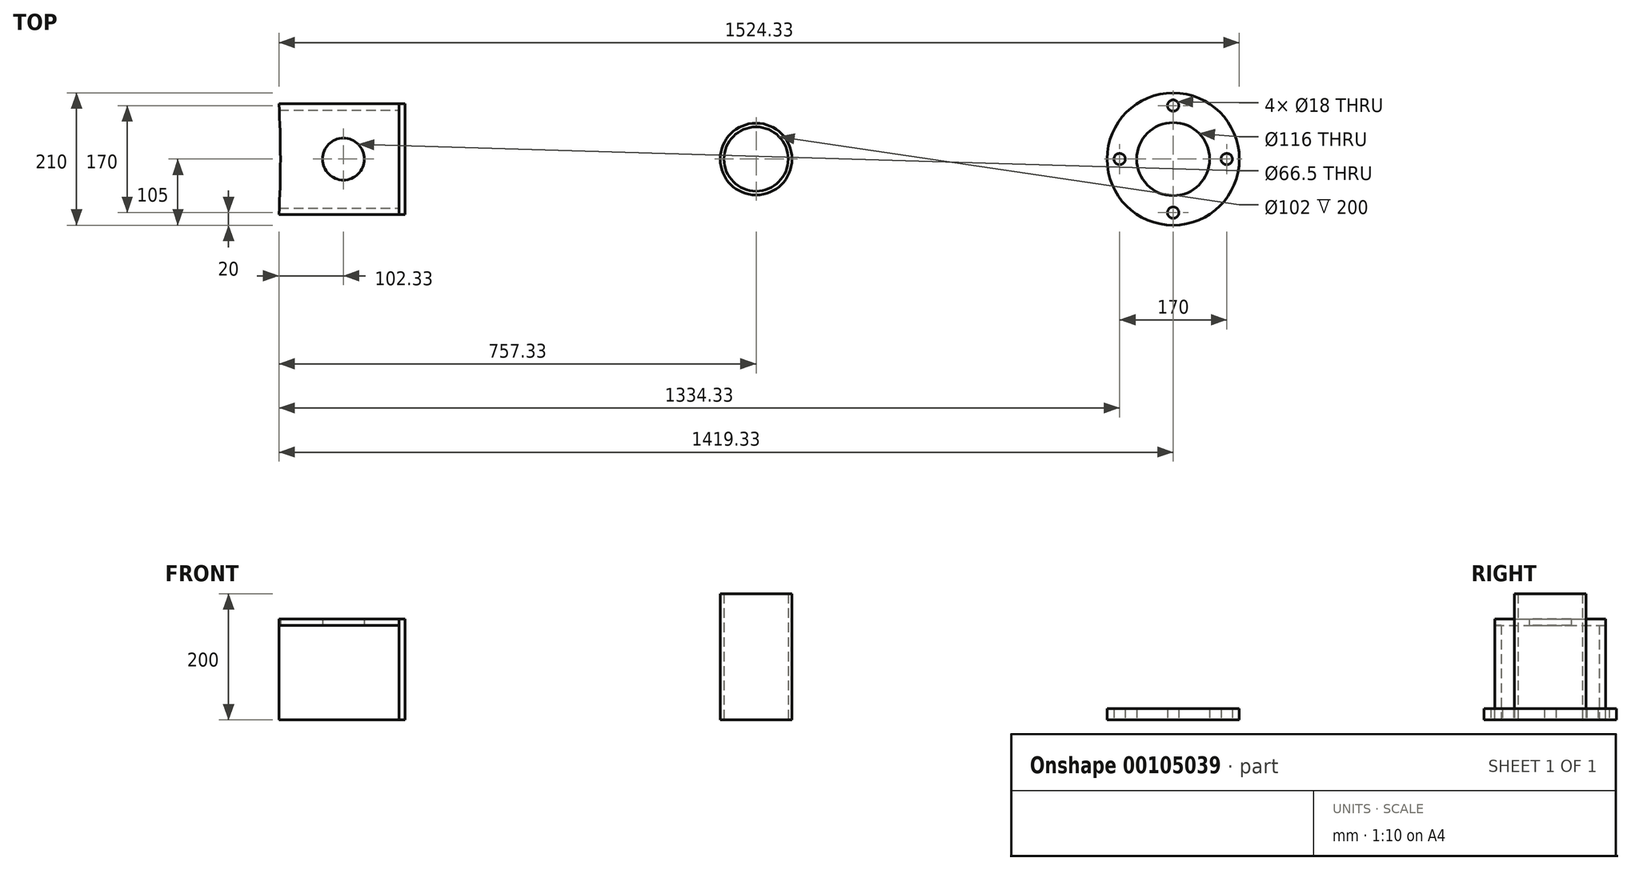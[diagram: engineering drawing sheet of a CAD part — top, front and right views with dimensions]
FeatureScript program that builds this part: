
annotation { "Feature Type Name" : "Feature", "Feature Type Description" : "" }
export const myFeature = defineFeature(function(context is Context, id is Id, definition is map)
    precondition{}
    {
        {
            var Q0;
            Q0=qCreatedBy(makeId("Top.planeOp"),FACE);
            var sketch = newSketch(context, id + "F0", { "sketchPlane" : qUnion([Q0])});
            skCircle(sketch, "E0", {"center": v(0, 0) * mm, "radius": 1665 * mm});
            skLineSegment(sketch, "E1", {"start": v(1663.17, 78) * mm, "end": v(1853, 78) * mm});
            skLineSegment(sketch, "E2", {"start": v(1853, 78) * mm, "end": v(1853, 88) * mm});
            skLineSegment(sketch, "E3", {"start": v(1853, 88) * mm, "end": v(1662.67, 88) * mm});
            skCircle(sketch, "E4", {"center": v(1765, 0) * mm, "radius": 58 * mm});
            skCircle(sketch, "E5", {"center": v(0, 0) * mm, "radius": 1677 * mm, "construction": true});
            skSolve(sketch);
        }
        {
            var Q0;
            {var subQ0=sQuery(id+"F0.wireOp",EDGE,"E1");Q0=makeQuery(id+"F0.imprint","IMPRINT",FACE,{"disambiguationData":[TD([[makeQuery(id+"F0.imprint","IMPRINT",EDGE,{"derivedFrom":subQ0}),1.0]])]});}
            extrude(context, id + "F1", {"entities" : qUnion([Q0]), "depth" : 150 * mm});
        }
        {
            var Q0;
            Q0=makeQuery(id+"F1.opExtrude","SWEPT_BODY",BODY,{"disambiguationData":[OSD([sQuery(id+"F0.wireOp",EDGE,"E0"),sQuery(id+"F0.wireOp",EDGE,"E1"),sQuery(id+"F0.wireOp",EDGE,"E2"),sQuery(id+"F0.wireOp",EDGE,"E3")])]});
            var Q1;
            Q1=qCreatedBy(makeId("Front.planeOp"),FACE);
            mirror(context, id + "F2", {"entities" : qUnion([Q0]), "mirrorPlane" : qUnion([Q1])});
        }
        {
            var Q0;
            Q0=makeQuery(id+"F1.opExtrude","CAP_FACE",FACE,{"disambiguationData":[OSD([sQuery(id+"F0.wireOp",EDGE,"E0"),sQuery(id+"F0.wireOp",EDGE,"E1"),sQuery(id+"F0.wireOp",EDGE,"E2"),sQuery(id+"F0.wireOp",EDGE,"E3")])],"isStart":false});
            var sketch = newSketch(context, id + "F3", { "sketchPlane" : qUnion([Q0])});
            skLineSegment(sketch, "E6", {"start": v(1662.67, 88) * mm, "end": v(1853, 88) * mm});
            skLineSegment(sketch, "E7", {"start": v(1853, 88) * mm, "end": v(1853, -88) * mm});
            skLineSegment(sketch, "E8", {"start": v(1853, -88) * mm, "end": v(1662.67, -88) * mm});
            skArc(sketch, "E9", {"start": v(1662.67, 88) * mm, "mid": v(1665, 0) * mm, "end": v(1662.67, -88) * mm});
            skCircle(sketch, "E10", {"center": v(1765, 0) * mm, "radius": 33.25 * mm});
            skSolve(sketch);
        }
        {
            var Q0;
            Q0=qSketchRegion(id+"F3",true);
            extrude(context, id + "F4", {"entities" : qUnion([Q0]), "depth" : 10 * mm});
        }
        {
            var Q0;
            Q0=makeQuery(id+"F2.opPattern","COPY",FACE,{"derivedFrom":makeQuery(id+"F1.opExtrude","SWEPT_FACE",FACE,{"disambiguationData":[OSD([sQuery(id+"F0.wireOp",EDGE,"E2")])]}),"instanceName":"1"});
            var sketch = newSketch(context, id + "F5", { "sketchPlane" : qUnion([Q0])});
            skLineSegment(sketch, "E11.bottom", {"start": v(-88, 0) * mm, "end": v(88, 0) * mm});
            skLineSegment(sketch, "E11.top", {"start": v(-88, 160) * mm, "end": v(88, 160) * mm});
            skLineSegment(sketch, "E11.left", {"start": v(-88, 0) * mm, "end": v(-88, 160) * mm});
            skLineSegment(sketch, "E11.right", {"start": v(88, 0) * mm, "end": v(88, 160) * mm});
            skSolve(sketch);
        }
        {
            var Q0;
            Q0=qSketchRegion(id+"F5",true);
            extrude(context, id + "F6", {"entities" : qUnion([Q0]), "depth" : 10 * mm});
        }
        {
            assignVariable(context, id + "F7", {"name" : "C6", "anyValue" : 18});
        }
        {
            assignVariable(context, id + "F8", {"name" : "C8", "anyValue" : 4});
        }
        {
            var Q0;
            Q0=qCreatedBy(makeId("Top.planeOp"),FACE);
            var sketch = newSketch(context, id + "F9", { "sketchPlane" : qUnion([Q0])});
            skCircle(sketch, "E12", {"center": v(2420, 0) * mm, "radius": 51 * mm});
            skCircle(sketch, "E13", {"center": v(2420, 0) * mm, "radius": 57 * mm});
            skCircle(sketch, "E14", {"center": v(3082, 0) * mm, "radius": 58 * mm});
            skCircle(sketch, "E15", {"center": v(3082, 0) * mm, "radius": 105 * mm});
            skCircle(sketch, "E16", {"center": v(3082, 0) * mm, "radius": 85 * mm, "construction": true});
            skCircle(sketch, "E17", {"center": v(3082, 85) * mm, "radius": 9 * mm});
            skSolve(sketch);
        }
        {
            var Q0;
            Q0=makeQuery(id+"F9.imprint","IMPRINT",FACE,{"disambiguationData":[TD([[makeQuery(id+"F9.imprint","IMPRINT",EDGE,{"derivedFrom":sQuery(id+"F9.wireOp",EDGE,"E12")}),-1.0]])]});
            extrude(context, id + "F10", {"entities" : qUnion([Q0]), "depth" : 200 * mm});
        }
        {
            var Q0;
            Q0=makeQuery(id+"F9.imprint","IMPRINT",FACE,{"disambiguationData":[TD([[makeQuery(id+"F9.imprint","IMPRINT",EDGE,{"derivedFrom":sQuery(id+"F9.wireOp",EDGE,"E14")}),-1.0]])]});
            extrude(context, id + "F11", {"entities" : qUnion([Q0]), "depth" : (getVariable(context, 'C6')) * mm});
        }
        {
            var Q0;
            Q0=makeQuery(id+"F11.opExtrude","SWEPT_FACE",FACE,{"disambiguationData":[OSD([sQuery(id+"F9.wireOp",EDGE,"E17")])]});
            var Q1;
            Q1=makeQuery(id+"F11.opExtrude","CAP_EDGE",EDGE,{"disambiguationData":[OSD([sQuery(id+"F9.wireOp",EDGE,"E14")])],"isStart":false});
            circularPattern(context, id + "F12", {"patternType" : PatternType.FACE, "faces" : qUnion([Q0]), "axis" : qUnion([Q1]), "angle" : 360 * degree, "instanceCount" : getVariable(context, 'C8'), "equalSpace" : true});
        }
    });
